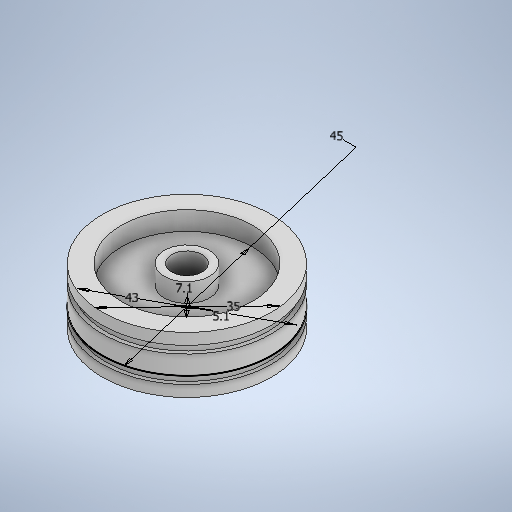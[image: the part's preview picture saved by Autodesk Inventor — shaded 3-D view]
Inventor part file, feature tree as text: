
AUTODESK INVENTOR PART (.ipt)
format: ipt  version: 2025.1 (Build 291241020, 241B)  size: 324,096 bytes
history: native  units: mm
features: extrude x9, sketch x3
ambient origin geometry x8: Origin, YZ Plane, XZ Plane, XY Plane, X Axis, Y Axis, Z Axis, Center Point
bodies: Solid1 (feature_tree)
feature tree (12):
  sketch  "Sketch1"  dims[d0=45.0mm d1=5.1mm]
  extrude  "Extrusion1"  Depth=5.1mm
  extrude  "Extrusion2"  Depth=5.0mm TaperAngle=0.0deg
  extrude  "Extrusion3"  Depth=5.0mm TaperAngle=0.0deg
  extrude  "Extrusion4"  Depth=15.0mm
  extrude  "Extrusion5"  Depth=2.0mm TaperAngle=0.0deg
  extrude  "Extrusion6"  Depth=15.0mm
  extrude  "Extrusion7"  Depth=15.0mm
  sketch  "Sketch3"  dims[d5=10.0mm d6=0.0mm d7=5.0mm d8=0.0mm d9=43.0mm d10=2.0mm d11=0.0mm d12=45.0mm d13=43.0mm d14=2.0mm d15=0.0mm d16=7.1mm d17=5.0mm d18=0.0mm d19=10.0mm d20=0.0mm d21=8.1mm d22=12.0mm d23=15.0mm d24=0.0mm d25=0.0mm d26=0.0mm]
  extrude  "Extrusion8"  Depth=2.0mm TaperAngle=0.0deg
  extrude  "Extrusion9"  Depth=15.0mm
  sketch  "Sketch2"  dims[d2=35.0mm d3=5.0mm d4=0.0mm]
